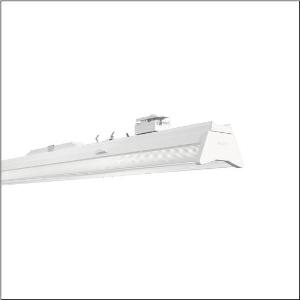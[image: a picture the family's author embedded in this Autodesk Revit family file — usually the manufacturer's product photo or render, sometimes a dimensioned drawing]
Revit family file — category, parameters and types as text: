
# Revit family: licross_r__21_performance_mo_52tm16dn4a5g_341e
name_source: partatom
category: Lighting Fixtures
units: mm (PartAtom-declared; Revit-internal decimal feet)

## family parameters
Cut with Voids When Loaded = No
Host = Face
Light Source = No
Part Type = Normal
Room Calculation Point = No
Round Connector Dimension = Use Diameter
Shared = No

## types (1)
- --- (1 x LED, 10840 lm, 62 W, 4000K)
    Apparent Load = 62 VA
    CIE Flux Codes = 66 88 96 79 100
    Color Rendering = 80
    Color Temperature = 4000K
    Default Elevation = 1800 mm
    Description = Licross® 21 Performance MO, luminaire insert, of sheet steel, galvanised, coil coated, white, length: 1.500mm, width: 120mm, height: 123mm, LED rated luminous flux: 10.840lm, light colour: 840, SDCM (Standard Deviation of Colour Matching)MacAdam ≤ 3 SDCM (initial), control gear: DALI 2, with plug, 5-pole, with phase selection, mains connection: 220..240V, AC, 50/60Hz, rated input power: 62W, internal wiring halogen-free, primary light control with lens, of plastic, primary optical cover: cover, of PMMA, light emission: direct/indirect distribution, primary light characteristic: symmetric, protection rating (complete): IP40, insulation class (complete): insulation class I (protective earthing), certification: CE, ENEC, UKCA, protection symbol: D if used in an environment without relevant dust loads with corresponding accessories, impact resistance: IK06, permissible ambient temperature for indoor applications: -25..+35°C, corresponds to IFS (International Featured Standards) requirements for safety and quality in the food industry, reducing of maximum allowable ambient temperature of 5°C with ceiling mounting, LABS conformity tested according to VDMA 24364:2018-05, packaging unit: 1 piece
    Height = 114 mm
    Lamp = 1 x LED
    Lamp Light Flux = 10840 lm
    Lamp Power = 62 W
    Lamp count = 1
    Length = 1500 mm
    Luminous efficacy = 175 lm/W
    Manufacturer = Siteco
    ModVariant = No
    Model = 52TM16DN4A5G
    Mounting Place = Ceiling
    Mounting Type = Pendant
    Number of Poles = 1
    OnlyDefault = Yes
    Power Factor = 1
    Product Name = Licross® 21 Performance MO
    Product group = luminaire insert | ceiling pendant
    ProductGroupID = 901
    Protection Class = Protection class I
    Protection Degree = IP 40
    RLX_Detail_Level = 1
    RLX_Emergency_Light_Flux = 0 lm
    RLX_Emergency_Type = 0
    RLX_Emergency_Type_DB = No
    RlxData = <blob elided: 34217 chars, md5=3e075c70>
    Socket = socket
    Standby Power = 0 W
    System Light Flux = 10840 lm
    System Power = 62 W
    Type Comments = factory setting: luminous flux: 100 % | dim-lin: 254 | 418 mA
    Type Image = l_1256138.jpg
    URL = http://relux.com
    VarID = @adj_133175
    Voltage = 0 V
    Weight = 0.00 kg
    Width = 120 mm

## geometry (parser evidence)
native form markers: Blend x4, Sweep x12
no freeform markers — native parametric forms only
